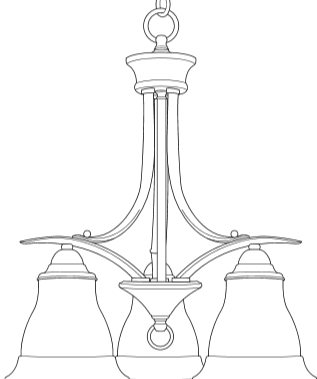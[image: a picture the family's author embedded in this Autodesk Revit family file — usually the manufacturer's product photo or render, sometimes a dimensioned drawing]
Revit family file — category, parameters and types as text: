
# Revit family: P4416-77 5-100W CHAND
name_source: partatom
category: Lighting Fixtures
revit_build: Autodesk Revit Architecture 2012 (Build: 20110309_2315(x64)
units: mm (PartAtom-declared; Revit-internal decimal feet)

## types (1)
- P4416-77 5-100W CHAND
    Ceiling Chain = Forged Bronze
    Celing chain length = 40"
    Chandelier = Forged Bronze
    Default Elevation = 48"
    Description = Five-light chandelier with tea stained oversized, bell-shaped glass bowls. Distinctive ebbing and flowing of squared scrolls and arms in Forged Bronze finish.
    Family = Torino
    Glass = Tea Stained Glass
    Lamp = Five
    Manufacturer = Progress Lighting
    Manufacturer Fax = 864-678-1065
    Model = P4416-77
    Product Documentation Link = http://progresslighting.com
    Product Page URL = http://progresslighting.com
    URL = http://progresslighting.com
    Wattage Comments = 100 W

## geometry (parser evidence)
native form markers: Sweep x7
no freeform markers — native parametric forms only
